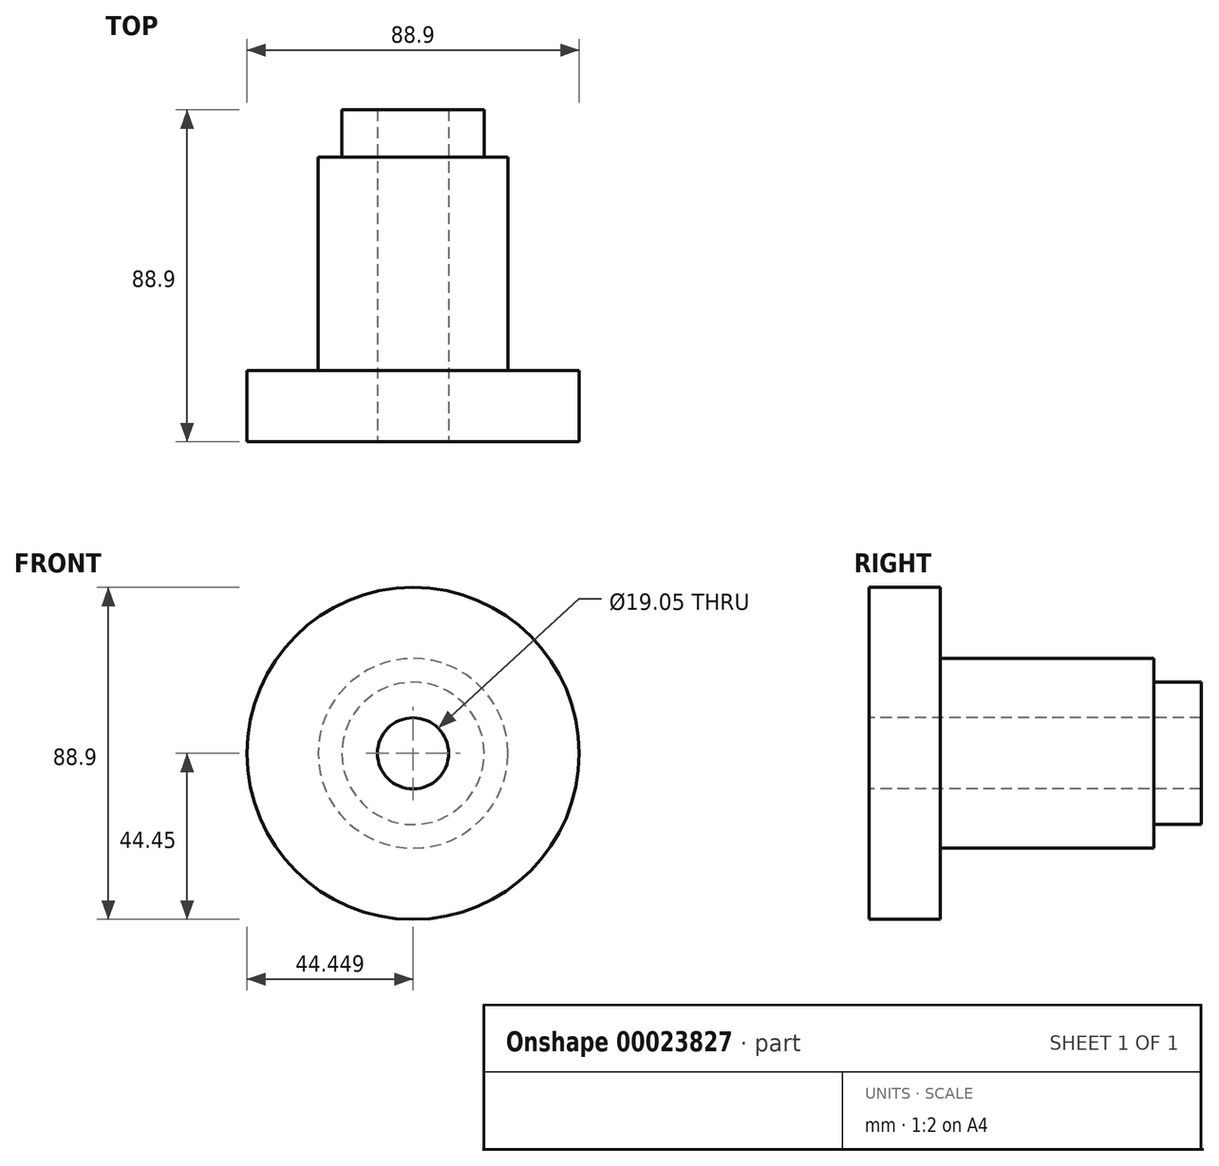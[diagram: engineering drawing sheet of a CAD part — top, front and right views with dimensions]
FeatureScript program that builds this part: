
annotation { "Feature Type Name" : "Feature", "Feature Type Description" : "" }
export const myFeature = defineFeature(function(context is Context, id is Id, definition is map)
    precondition{}
    {
        {
            var Q0;
            Q0=qCreatedBy(makeId("Top.planeOp"),FACE);
            var sketch = newSketch(context, id + "F0", { "sketchPlane" : qUnion([Q0])});
            skLineSegment(sketch, "E0.bottom", {"start": v(-235.2, -42.81) * mm, "end": v(-200.27, -42.81) * mm});
            skLineSegment(sketch, "E0.top", {"start": v(-235.2, -23.76) * mm, "end": v(-200.27, -23.76) * mm});
            skLineSegment(sketch, "E0.left", {"start": v(-235.2, -42.81) * mm, "end": v(-235.2, -23.76) * mm});
            skLineSegment(sketch, "E0.right", {"start": v(-200.27, -42.81) * mm, "end": v(-200.27, -23.76) * mm});
            skLineSegment(sketch, "E1.bottom", {"start": v(-200.27, -23.76) * mm, "end": v(-216.14, -23.76) * mm});
            skLineSegment(sketch, "E1.top", {"start": v(-200.27, 33.39) * mm, "end": v(-216.14, 33.39) * mm});
            skLineSegment(sketch, "E1.left", {"start": v(-200.27, -23.76) * mm, "end": v(-200.27, 33.39) * mm});
            skLineSegment(sketch, "E1.right", {"start": v(-216.14, -23.76) * mm, "end": v(-216.14, 33.39) * mm});
            skLineSegment(sketch, "E2.bottom", {"start": v(-200.27, 33.39) * mm, "end": v(-209.8, 33.39) * mm});
            skLineSegment(sketch, "E2.top", {"start": v(-200.27, 46.09) * mm, "end": v(-209.8, 46.09) * mm});
            skLineSegment(sketch, "E2.left", {"start": v(-200.27, 33.39) * mm, "end": v(-200.27, 46.09) * mm});
            skLineSegment(sketch, "E2.right", {"start": v(-209.8, 33.39) * mm, "end": v(-209.8, 46.09) * mm});
            skLineSegment(sketch, "E3", {"start": v(-190.74, -70.77) * mm, "end": v(-190.74, 57.62) * mm, "construction": true});
            skSolve(sketch);
        }
        {
            var Q0;
            Q0 = qSketchRegion(id + "F0", true);
            var Q1;
            Q1=sQuery(id+"F0.wireOp",EDGE,"E3");
            revolve(context, id + "F1", {"entities" : qUnion([Q0]), "axis" : qUnion([Q1]), "revolveType" : RevolveType.FULL});
        }
    });
